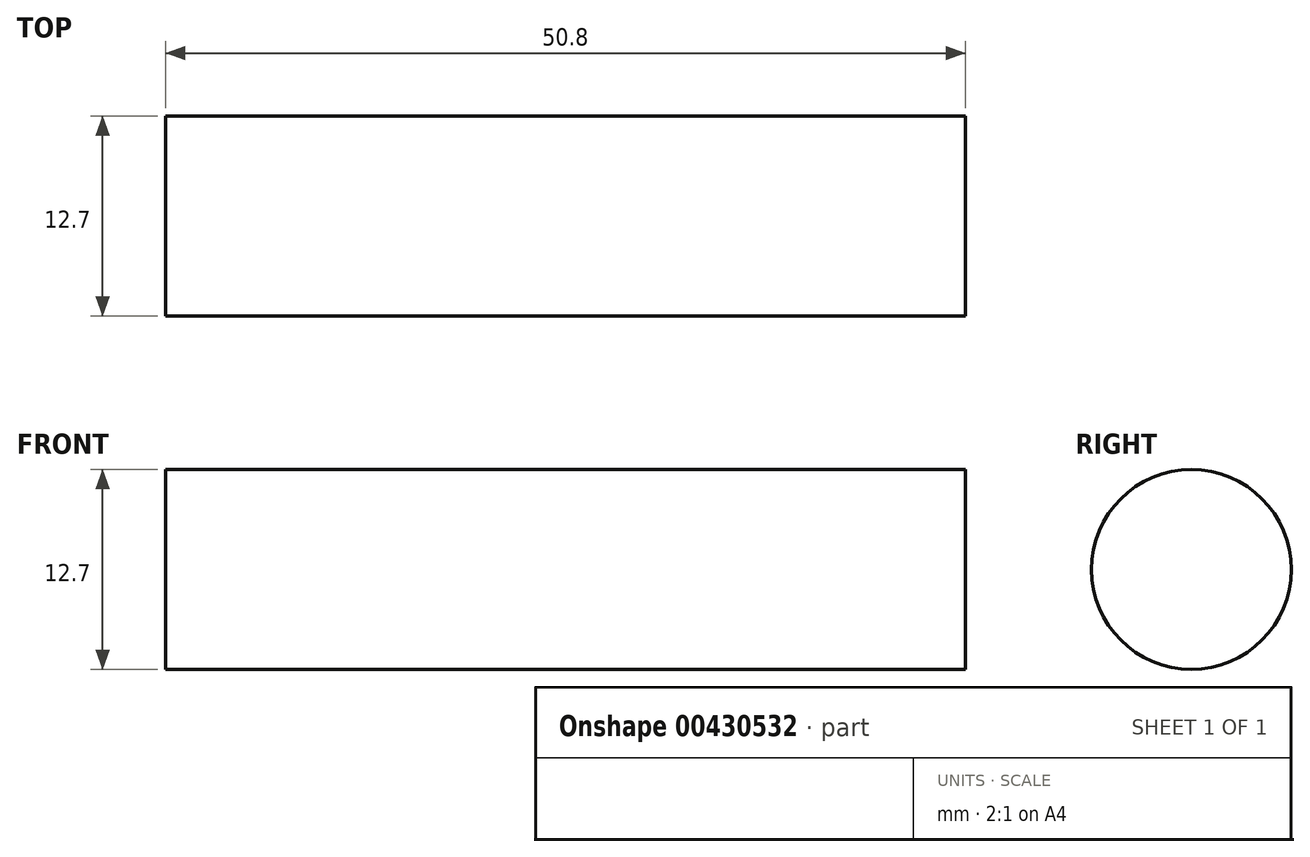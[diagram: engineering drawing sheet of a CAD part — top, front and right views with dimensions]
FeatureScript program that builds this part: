
annotation { "Feature Type Name" : "Feature", "Feature Type Description" : "" }
export const myFeature = defineFeature(function(context is Context, id is Id, definition is map)
    precondition{}
    {
        {
            var Q0;
            Q0=qCreatedBy(makeId("Right.planeOp"),FACE);
            var sketch = newSketch(context, id + "F0", { "sketchPlane" : qUnion([Q0])});
            skCircle(sketch, "E0", {"center": v(0, 0) * mm, "radius": 6.35 * mm});
            skSolve(sketch);
        }
        {
            var Q0;
            Q0=makeQuery(id+"F0.imprint","IMPRINT",FACE,{"disambiguationData":[TD([[makeQuery(id+"F0.imprint","IMPRINT",EDGE,{"derivedFrom":sQuery(id+"F0.wireOp",EDGE,"E0")}),1.0]])]});
            extrude(context, id + "F1", {"entities" : qUnion([Q0]), "depth" : 50.8 * mm});
        }
    });
